# Revit family: equip-water-cooler-hlsy-tylr-hvr-jo-60hz
name_source: partatom
category: Plumbing Fixtures
units: mm (PartAtom-declared; Revit-internal decimal feet)

## family parameters
Always vertical = Yes
Cut with Voids When Loaded = No
OmniClass Number = 23.45.00.00
OmniClass Title = Sanitary, Laundry, and Cleaning Equipment
Part Type = Normal
Room Calculation Point = No
Round Connector Dimension = Use Radius
Shared = No
Work Plane-Based = No

## types (4) — shared parameters
Activation = All include VR Pushbutton
Basin Material = Metal - Steel - Stainless - Chrome
Bubbler = All Include VR Bubbler
CW Connection = Yes
Cooler Bottom = 1' - 0 5/16"
Cooler Depth = 1' - 6 5/8"
Cooler Height = 1' - 8 5/8"
Cooler Rear Panel Depth = 0' - 6 27/32"
Cooler Width = 1' - 6 1/16"
Description = ADA Vandal Resistant Cooler
Dispenser Depth = 0' - 8"
Dispenser Height = 2' - 3"
Glass Filter = -
HW Connection = No
Manufacturer = Halsey Taylor
Orifice Height = 2' - 8 15/16"
Orifice to Rim = 0' - 1 13/16"
Other Features = VR pinned torx screws
Panel Material = Metal - Steel - Stainless - Color 1
Refrigerated = Yes
Rim Height = 2' - 7 1/8"
Rim to Dispenser = 0' - 4 1/8"
Type = Single
URL = http://www.halseytaylor.com
Vent Connection = No
Version = 1.0.0.0
Volts/Hertz = 220V/60Hz
Waste Connection = Yes
Water Service Flow = 0 GPM
Water Service Size Radius = 0' - 0 1/4"

## per-type parameters (varying)
| type | Filter | Louver Screens | Product ID |
| HVR8 | - | - | 8250089783 |
| HVR8-S | - | Yes | 82500897S83 |
| HVR8-WF | HWF172 | - | 8250082483 |
| HVR8-S-WF | HWF172 | Yes | 82500824S83 |

note: column(s) folded — value = type name in every type: Model

## geometry (parser evidence)
native form markers: Extrusion x1, Sweep x4
no freeform markers — native parametric forms only
